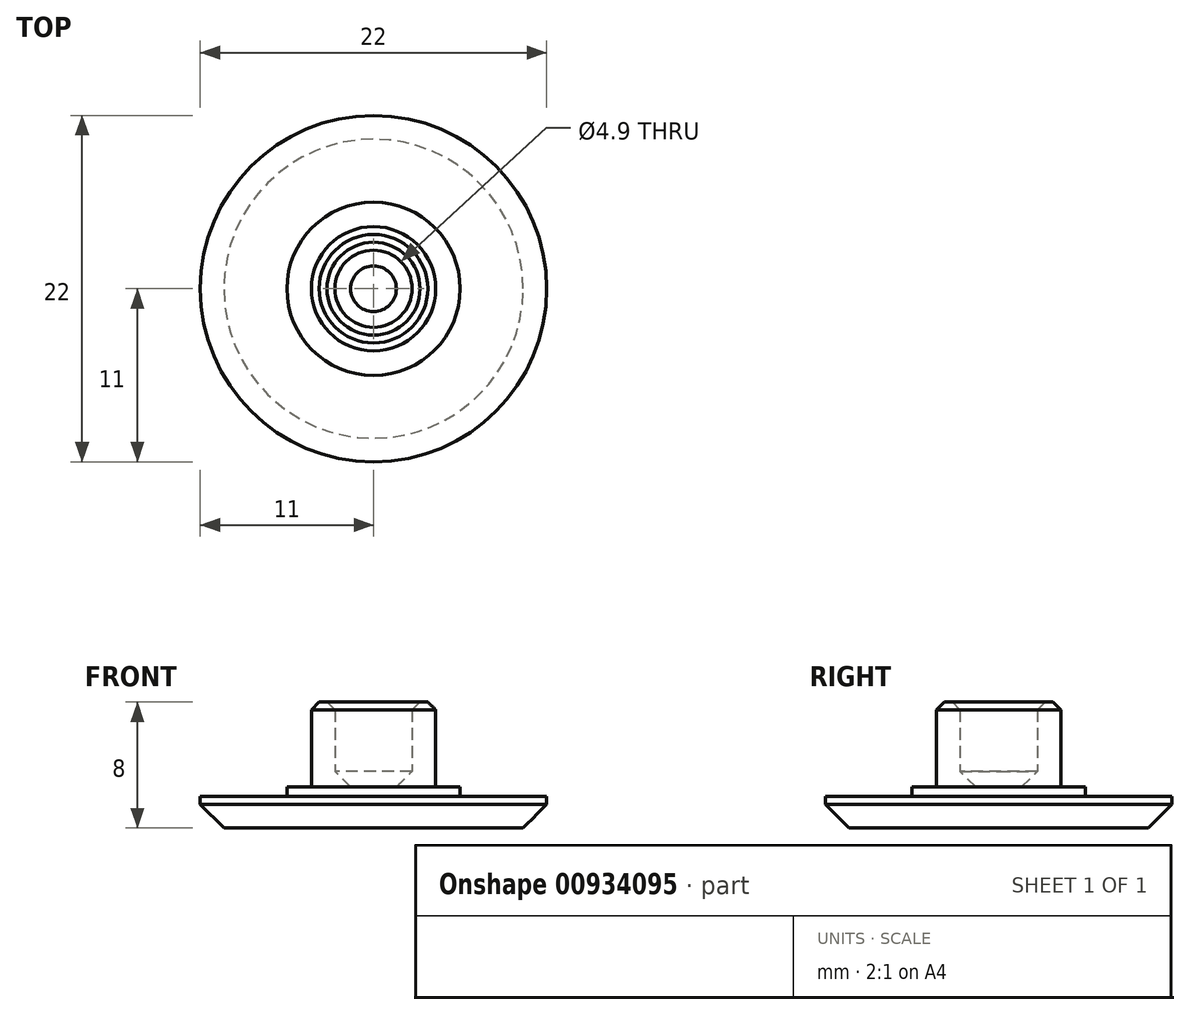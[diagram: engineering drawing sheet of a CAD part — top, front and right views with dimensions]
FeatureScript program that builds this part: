
annotation { "Feature Type Name" : "Feature", "Feature Type Description" : "" }
export const myFeature = defineFeature(function(context is Context, id is Id, definition is map)
    precondition{}
    {
        {
            var Q0;
            Q0=qCreatedBy(makeId("Top.planeOp"),FACE);
            var sketch = newSketch(context, id + "F0", { "sketchPlane" : qUnion([Q0])});
            skCircle(sketch, "E0", {"center": v(0, 0) * mm, "radius": 11 * mm});
            skCircle(sketch, "E1", {"center": v(0, 0) * mm, "radius": 3.95 * mm});
            skCircle(sketch, "E2", {"center": v(0, 0) * mm, "radius": 2.45 * mm});
            skCircle(sketch, "E3", {"center": v(0, 0) * mm, "radius": 5.5 * mm});
            skSolve(sketch);
        }
        {
            var Q0;
            Q0=makeQuery(id+"F0.imprint","IMPRINT",FACE,{"disambiguationData":[TD([[makeQuery(id+"F0.imprint","IMPRINT",EDGE,{"derivedFrom":sQuery(id+"F0.wireOp",EDGE,"E0")}),1.0]])]});
            var Q1;
            Q1=makeQuery(id+"F0.imprint","IMPRINT",FACE,{"disambiguationData":[TD([[makeQuery(id+"F0.imprint","IMPRINT",EDGE,{"derivedFrom":sQuery(id+"F0.wireOp",EDGE,"E1")}),-1.0]])]});
            var Q2;
            Q2=makeQuery(id+"F0.imprint","IMPRINT",FACE,{"disambiguationData":[TD([[makeQuery(id+"F0.imprint","IMPRINT",EDGE,{"derivedFrom":sQuery(id+"F0.wireOp",EDGE,"E1")}),1.0]])]});
            var Q3;
            Q3=makeQuery(id+"F0.imprint","IMPRINT",FACE,{"disambiguationData":[TD([[makeQuery(id+"F0.imprint","IMPRINT",EDGE,{"derivedFrom":sQuery(id+"F0.wireOp",EDGE,"E2")}),1.0]])]});
            var Q4;
            Q4=makeQuery(id+"F0.imprint","IMPRINT",FACE,{"disambiguationData":[TD([[makeQuery(id+"F0.imprint","IMPRINT",EDGE,{"derivedFrom":sQuery(id+"F0.wireOp",EDGE,"6H3RFypV-7Wqe-ZQjq-WIxb-NjeoeY7dnm9J")}),1.0]])]});
            extrude(context, id + "F1", {"entities" : qUnion([Q0, Q1, Q2, Q3, Q4]), "depth" : 2 * mm, "offsetDistance" : 25 * mm});
        }
        {
            var Q0;
            Q0=makeQuery(id+"F0.imprint","IMPRINT",FACE,{"disambiguationData":[TD([[makeQuery(id+"F0.imprint","IMPRINT",EDGE,{"derivedFrom":sQuery(id+"F0.wireOp",EDGE,"E1")}),1.0]])]});
            var Q1;
            Q1=makeQuery(id+"F0.imprint","IMPRINT",FACE,{"disambiguationData":[TD([[makeQuery(id+"F0.imprint","IMPRINT",EDGE,{"derivedFrom":sQuery(id+"F0.wireOp",EDGE,"E1")}),-1.0]])]});
            var Q2;
            Q2=makeQuery(id+"F0.imprint","IMPRINT",FACE,{"disambiguationData":[TD([[makeQuery(id+"F0.imprint","IMPRINT",EDGE,{"derivedFrom":sQuery(id+"F0.wireOp",EDGE,"E2")}),1.0]])]});
            var Q3;
            Q3=makeQuery(id+"F0.imprint","IMPRINT",FACE,{"disambiguationData":[TD([[makeQuery(id+"F0.imprint","IMPRINT",EDGE,{"derivedFrom":sQuery(id+"F0.wireOp",EDGE,"6H3RFypV-7Wqe-ZQjq-WIxb-NjeoeY7dnm9J")}),1.0]])]});
            extrude(context, id + "F2", {"entities" : qUnion([Q0, Q1, Q2, Q3]), "operationType" : NewBodyOperationType.ADD, "depth" : 2.6 * mm, "offsetDistance" : 25 * mm});
        }
        {
            var Q0;
            Q0=makeQuery(id+"F0.imprint","IMPRINT",FACE,{"disambiguationData":[TD([[makeQuery(id+"F0.imprint","IMPRINT",EDGE,{"derivedFrom":sQuery(id+"F0.wireOp",EDGE,"E1")}),1.0]])]});
            extrude(context, id + "F3", {"entities" : qUnion([Q0]), "operationType" : NewBodyOperationType.ADD, "depth" : 8 * mm, "offsetDistance" : 25 * mm});
        }
        {
            var Q0;
            Q0=makeQuery(id+"F3.opExtrude","CAP_EDGE",EDGE,{"disambiguationData":[OSD([sQuery(id+"F0.wireOp",EDGE,"E2")])],"isStart":false});
            chamfer(context, id + "F4", {"entities" : qUnion([Q0]), "width" : 0.5 * mm, "tangentPropagation" : true});
        }
        {
            var Q0;
            Q0=makeQuery(id+"F3.opExtrude","CAP_EDGE",EDGE,{"disambiguationData":[OSD([sQuery(id+"F0.wireOp",EDGE,"E1")])],"isStart":false});
            chamfer(context, id + "F5", {"entities" : qUnion([Q0]), "width" : 0.5 * mm, "tangentPropagation" : true});
        }
        {
            var Q0;
            Q0=makeQuery(id+"F1.opExtrude","CAP_EDGE",EDGE,{"disambiguationData":[OSD([sQuery(id+"F0.wireOp",EDGE,"E0")])],"isStart":true});
            chamfer(context, id + "F6", {"entities" : qUnion([Q0]), "width" : 1.5 * mm, "tangentPropagation" : true});
        }
        {
            var Q0;
            Q0=makeQuery(id+"F3.boolean.opBoolean","INTERSECT",EDGE,{"derivedFrom":[makeQuery(id+"F2.opExtrude","CAP_FACE",FACE,{"disambiguationData":[OSD([sQuery(id+"F0.wireOp",EDGE,"E3")])],"isStart":false}),makeQuery(id+"F3.opExtrude","SWEPT_FACE",FACE,{"disambiguationData":[OSD([sQuery(id+"F0.wireOp",EDGE,"E2")])]})]});
            chamfer(context, id + "F7", {"entities" : qUnion([Q0]), "width" : 1 * mm, "tangentPropagation" : true});
        }
    });
